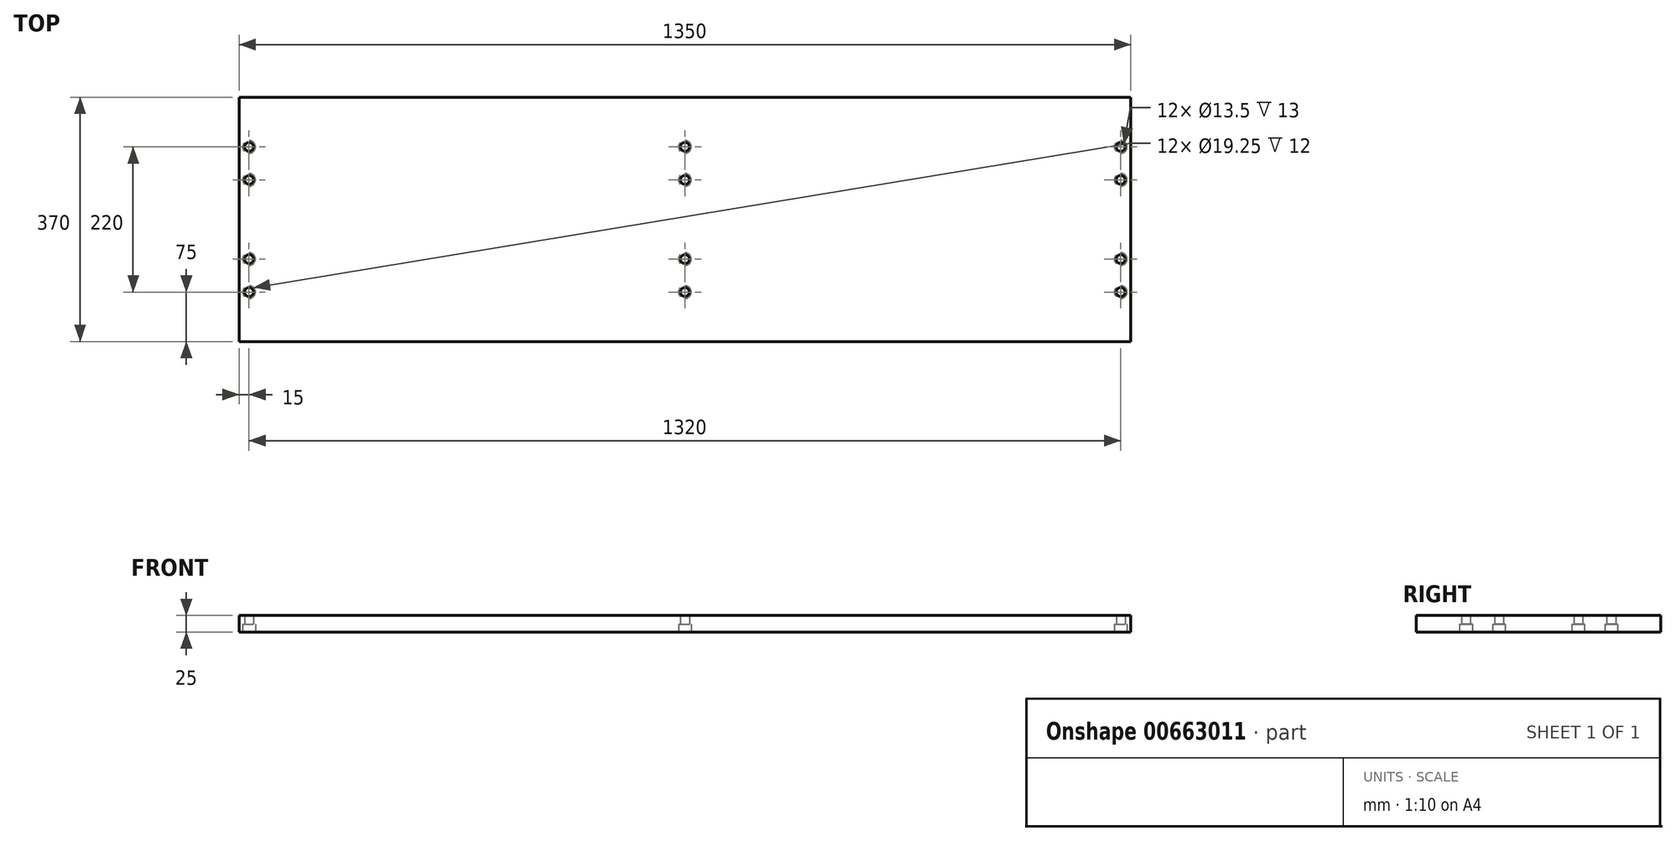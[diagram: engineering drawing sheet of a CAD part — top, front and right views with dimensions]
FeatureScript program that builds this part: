
annotation { "Feature Type Name" : "Feature", "Feature Type Description" : "" }
export const myFeature = defineFeature(function(context is Context, id is Id, definition is map)
    precondition{}
    {
        {
            var Q0;
            Q0=qCreatedBy(makeId("Top.planeOp"),FACE);
            var sketch = newSketch(context, id + "F0", { "sketchPlane" : qUnion([Q0])});
            skLineSegment(sketch, "E0.bottom", {"start": v(675, -185) * mm, "end": v(-675, -185) * mm});
            skLineSegment(sketch, "E0.top", {"start": v(675, 185) * mm, "end": v(-675, 185) * mm});
            skLineSegment(sketch, "E0.left", {"start": v(675, -185) * mm, "end": v(675, 185) * mm});
            skLineSegment(sketch, "E0.right", {"start": v(-675, -185) * mm, "end": v(-675, 185) * mm});
            skPoint(sketch, "E0.middle", {"position": v(0, 0) * mm});
            skSolve(sketch);
        }
        {
            var Q0;
            Q0=makeQuery(id+"F0.imprint","IMPRINT",FACE,{"disambiguationData":[TD([[makeQuery(id+"F0.imprint","IMPRINT",EDGE,{"derivedFrom":sQuery(id+"F0.wireOp",EDGE,"E0.bottom")}),-1.0]])]});
            extrude(context, id + "F1", {"entities" : qUnion([Q0]), "depth" : 25 * mm, "offsetDistance" : 25 * mm});
        }
        {
            var Q0;
            Q0=makeQuery(id+"F1.opExtrude","CAP_FACE",FACE,{"disambiguationData":[OSD([sQuery(id+"F0.wireOp",EDGE,"E0.bottom"),sQuery(id+"F0.wireOp",EDGE,"E0.top"),sQuery(id+"F0.wireOp",EDGE,"E0.left"),sQuery(id+"F0.wireOp",EDGE,"E0.right")])],"isStart":true});
            var sketch = newSketch(context, id + "F2", { "sketchPlane" : qUnion([Q0])});
            skPoint(sketch, "E1", {"position": v(-660, 110) * mm});
            skPoint(sketch, "E2", {"position": v(-660, 60) * mm});
            skPoint(sketch, "E3", {"position": v(-660, -60) * mm});
            skPoint(sketch, "E4", {"position": v(-660, -110) * mm});
            skPoint(sketch, "E5", {"position": v(0, 110) * mm});
            skPoint(sketch, "E6", {"position": v(0, 60) * mm});
            skPoint(sketch, "E7", {"position": v(0, -60) * mm});
            skPoint(sketch, "E8", {"position": v(0, -110) * mm});
            skPoint(sketch, "E9", {"position": v(660, 110) * mm});
            skPoint(sketch, "E10", {"position": v(660, 60) * mm});
            skPoint(sketch, "E11", {"position": v(660, -60) * mm});
            skPoint(sketch, "E12", {"position": v(660, -110) * mm});
            skLineSegment(sketch, "E13", {"start": v(-660, 110) * mm, "end": v(0, 110) * mm, "construction": true});
            skLineSegment(sketch, "E14", {"start": v(0, 110) * mm, "end": v(660, 110) * mm, "construction": true});
            skLineSegment(sketch, "E15", {"start": v(0, 60) * mm, "end": v(0, 110) * mm, "construction": true});
            skLineSegment(sketch, "E16", {"start": v(0, -110) * mm, "end": v(660, -110) * mm, "construction": true});
            skLineSegment(sketch, "E17", {"start": v(0, -60) * mm, "end": v(660, -60) * mm, "construction": true});
            skLineSegment(sketch, "E18", {"start": v(0, -60) * mm, "end": v(-660, -60) * mm, "construction": true});
            skLineSegment(sketch, "E19", {"start": v(-660, -110) * mm, "end": v(0, -110) * mm, "construction": true});
            skLineSegment(sketch, "E20", {"start": v(0, 60) * mm, "end": v(-660, 60) * mm, "construction": true});
            skLineSegment(sketch, "E21", {"start": v(660, 60) * mm, "end": v(0, 60) * mm, "construction": true});
            skLineSegment(sketch, "E22", {"start": v(660, 110) * mm, "end": v(660, 60) * mm, "construction": true});
            skLineSegment(sketch, "E23", {"start": v(660, 60) * mm, "end": v(660, -60) * mm, "construction": true});
            skLineSegment(sketch, "E24", {"start": v(660, -60) * mm, "end": v(660, -110) * mm, "construction": true});
            skLineSegment(sketch, "E25", {"start": v(-660, -110) * mm, "end": v(-660, -60) * mm, "construction": true});
            skLineSegment(sketch, "E26", {"start": v(-660, -60) * mm, "end": v(-660, 60) * mm, "construction": true});
            skLineSegment(sketch, "E27", {"start": v(-660, 60) * mm, "end": v(-660, 110) * mm, "construction": true});
            skLineSegment(sketch, "E28", {"start": v(-660, -110) * mm, "end": v(-660, -185) * mm, "construction": true});
            skLineSegment(sketch, "E29", {"start": v(-660, 110) * mm, "end": v(-660, 185) * mm, "construction": true});
            skSolve(sketch);
        }
        {
            var Q0;
            Q0=sQuery(id+"F2.wireOp",VERTEX,"E1");
            var Q1;
            Q1=sQuery(id+"F2.wireOp",VERTEX,"E20.end");
            var Q2;
            Q2=sQuery(id+"F2.wireOp",VERTEX,"E5");
            var Q3;
            Q3=sQuery(id+"F2.wireOp",VERTEX,"E6");
            var Q4;
            Q4=sQuery(id+"F2.wireOp",VERTEX,"E10");
            var Q5;
            Q5=sQuery(id+"F2.wireOp",VERTEX,"E9");
            var Q6;
            Q6=sQuery(id+"F2.wireOp",VERTEX,"E12");
            var Q7;
            Q7=sQuery(id+"F2.wireOp",VERTEX,"E11");
            var Q8;
            Q8=sQuery(id+"F2.wireOp",VERTEX,"E7");
            var Q9;
            Q9=sQuery(id+"F2.wireOp",VERTEX,"E8");
            var Q10;
            Q10=sQuery(id+"F2.wireOp",VERTEX,"E19.start");
            var Q11;
            Q11=sQuery(id+"F2.wireOp",VERTEX,"E3");
            var Q12;
            Q12=makeQuery(id+"F1.opExtrude","SWEPT_BODY",BODY,{"disambiguationData":[OSD([sQuery(id+"F0.wireOp",EDGE,"E0.bottom"),sQuery(id+"F0.wireOp",EDGE,"E0.top"),sQuery(id+"F0.wireOp",EDGE,"E0.left"),sQuery(id+"F0.wireOp",EDGE,"E0.right")])]});
            hole(context, id + "F3", {"style" : HoleStyle.C_BORE, "endStyle" : HoleEndStyle.THROUGH, "standardTappedOrClearance" : lookupTablePath({ "fit" : "Normal", "standard" : "ISO", "size" : "M12", "type" : "Clearance" }), "standardBlindInLast" : lookupTablePath({ "fit" : "Normal", "standard" : "ISO", "engagement" : "75%", "pitch" : "1.75 mm", "size" : "M12", "type" : "Clearance & tapped" }), "holeDiameter" : 13.5 * mm, "cBoreDiameter" : 19.25 * mm, "cBoreDepth" : 12 * mm, "majorDiameter" : 12 * mm, "isTappedThrough" : true, "tappedDepth" : 12 * mm, "tapClearance" : 3, "locations" : qUnion([Q0, Q1, Q2, Q3, Q4, Q5, Q6, Q7, Q8, Q9, Q10, Q11]), "scope" : qUnion([Q12])});
        }
    });
